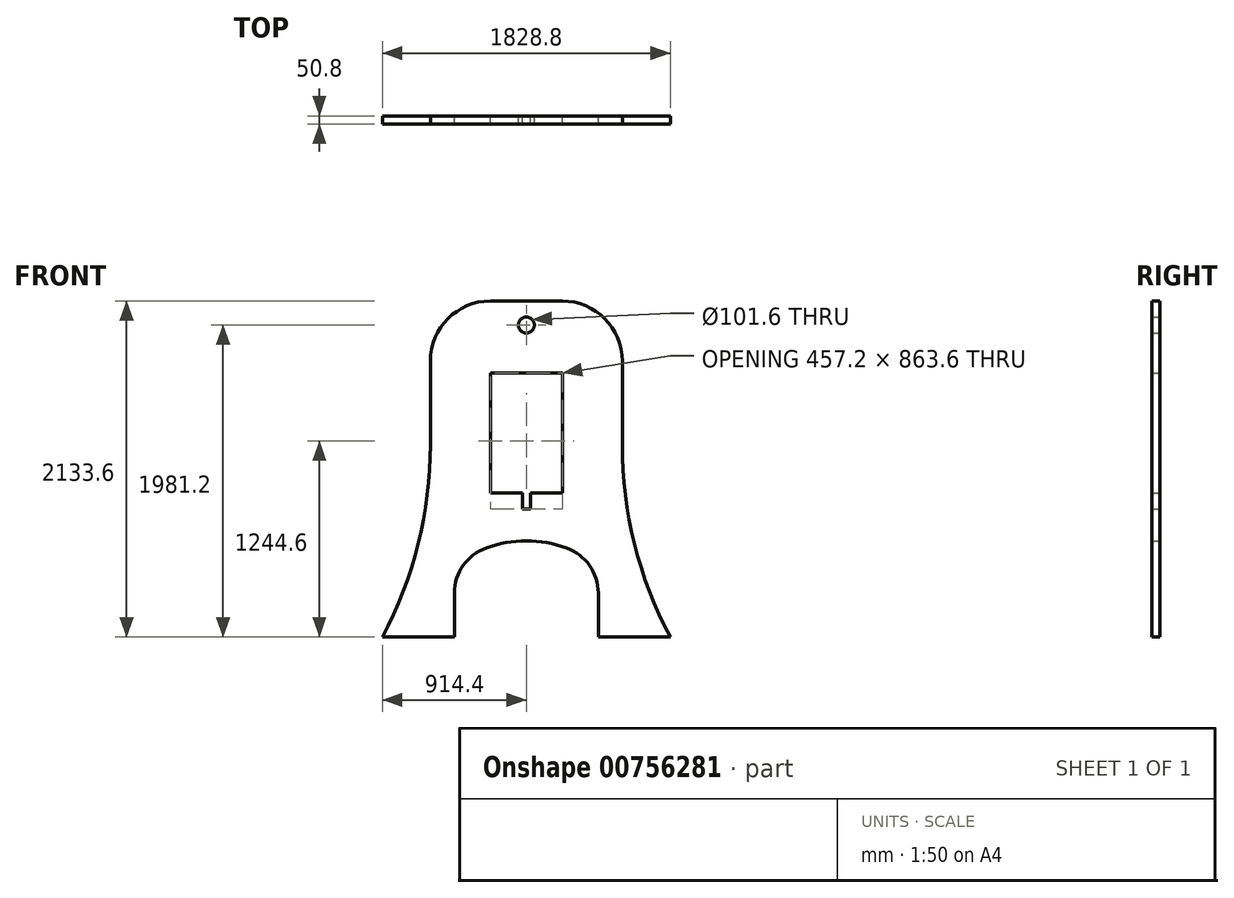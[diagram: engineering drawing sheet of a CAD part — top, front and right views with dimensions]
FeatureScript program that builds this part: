
annotation { "Feature Type Name" : "Feature", "Feature Type Description" : "" }
export const myFeature = defineFeature(function(context is Context, id is Id, definition is map)
    precondition{}
    {
        {
            var Q0;
            Q0=qCreatedBy(makeId("Front.planeOp"),FACE);
            var sketch = newSketch(context, id + "F0", { "sketchPlane" : qUnion([Q0])});
            skLineSegment(sketch, "E0", {"start": v(838.2, 2133.6) * mm, "end": v(381, 2133.6) * mm});
            skLineSegment(sketch, "E1", {"start": v(381, 914.4) * mm, "end": v(381, 1676.4) * mm});
            skLineSegment(sketch, "E2", {"start": v(381, 1676.4) * mm, "end": v(838.2, 1676.4) * mm});
            skLineSegment(sketch, "E3", {"start": v(838.2, 1676.4) * mm, "end": v(838.2, 914.4) * mm});
            skPoint(sketch, "E4.visualSharp", {"position": v(0, 2133.6) * mm});
            skArc(sketch, "E4.filletArc", {"start": v(381, 2133.6) * mm, "mid": v(111.6, 2022) * mm, "end": v(0, 1752.6) * mm});
            skPoint(sketch, "E5.visualSharp", {"position": v(1219.2, 2133.6) * mm});
            skArc(sketch, "E5.filletArc", {"start": v(1219.2, 1752.6) * mm, "mid": v(1107.6, 2022) * mm, "end": v(838.2, 2133.6) * mm});
            skCircle(sketch, "E6", {"center": v(609.6, 1981.2) * mm, "radius": 50.8 * mm});
            skArc(sketch, "E7", {"start": v(-304.8, 0) * mm, "mid": v(-77.35, 590.84) * mm, "end": v(0, 1219.2) * mm});
            skArc(sketch, "E8", {"start": v(1219.2, 1219.2) * mm, "mid": v(1296.55, 590.84) * mm, "end": v(1524, 0) * mm});
            skLineSegment(sketch, "E9", {"start": v(0, 1752.6) * mm, "end": v(0, 1219.2) * mm});
            skLineSegment(sketch, "E10", {"start": v(1219.2, 1752.6) * mm, "end": v(1219.2, 1219.2) * mm});
            skLineSegment(sketch, "E11", {"start": v(152.4, 0) * mm, "end": v(152.4, 278.65) * mm});
            skLineSegment(sketch, "E12", {"start": v(1066.8, 278.65) * mm, "end": v(1066.8, 0) * mm});
            skArc(sketch, "E13", {"start": v(863.6, 566.02) * mm, "mid": v(609.6, 609.6) * mm, "end": v(355.6, 566.02) * mm});
            skLineSegment(sketch, "E14", {"start": v(-304.8, 0) * mm, "end": v(152.4, 0) * mm});
            skLineSegment(sketch, "E15", {"start": v(1066.8, 0) * mm, "end": v(1524, 0) * mm});
            skPoint(sketch, "E16.visualSharp", {"position": v(152.4, 457.2) * mm});
            skArc(sketch, "E16.filletArc", {"start": v(355.6, 566.02) * mm, "mid": v(208.33, 454.63) * mm, "end": v(152.4, 278.65) * mm});
            skPoint(sketch, "E17.visualSharp", {"position": v(1066.8, 457.2) * mm});
            skArc(sketch, "E17.filletArc", {"start": v(1066.8, 278.65) * mm, "mid": v(1010.87, 454.63) * mm, "end": v(863.6, 566.02) * mm});
            skLineSegment(sketch, "E18", {"start": v(584.2, 914.4) * mm, "end": v(584.2, 812.8) * mm});
            skLineSegment(sketch, "E19", {"start": v(584.2, 812.8) * mm, "end": v(635, 812.8) * mm});
            skLineSegment(sketch, "E20", {"start": v(635, 812.8) * mm, "end": v(635, 914.4) * mm});
            skLineSegment(sketch, "E21", {"start": v(381, 914.4) * mm, "end": v(584.2, 914.4) * mm});
            skLineSegment(sketch, "E22", {"start": v(635, 914.4) * mm, "end": v(838.2, 914.4) * mm});
            skSolve(sketch);
        }
        {
            var Q0;
            Q0=makeQuery(id+"F0.imprint","IMPRINT",FACE,{"disambiguationData":[TD([[makeQuery(id+"F0.imprint","IMPRINT",EDGE,{"derivedFrom":sQuery(id+"F0.wireOp",EDGE,"E0")}),1.0]])]});
            extrude(context, id + "F1", {"entities" : qUnion([Q0]), "depth" : 50.8 * mm, "offsetDistance" : 25.4 * mm});
        }
    });
